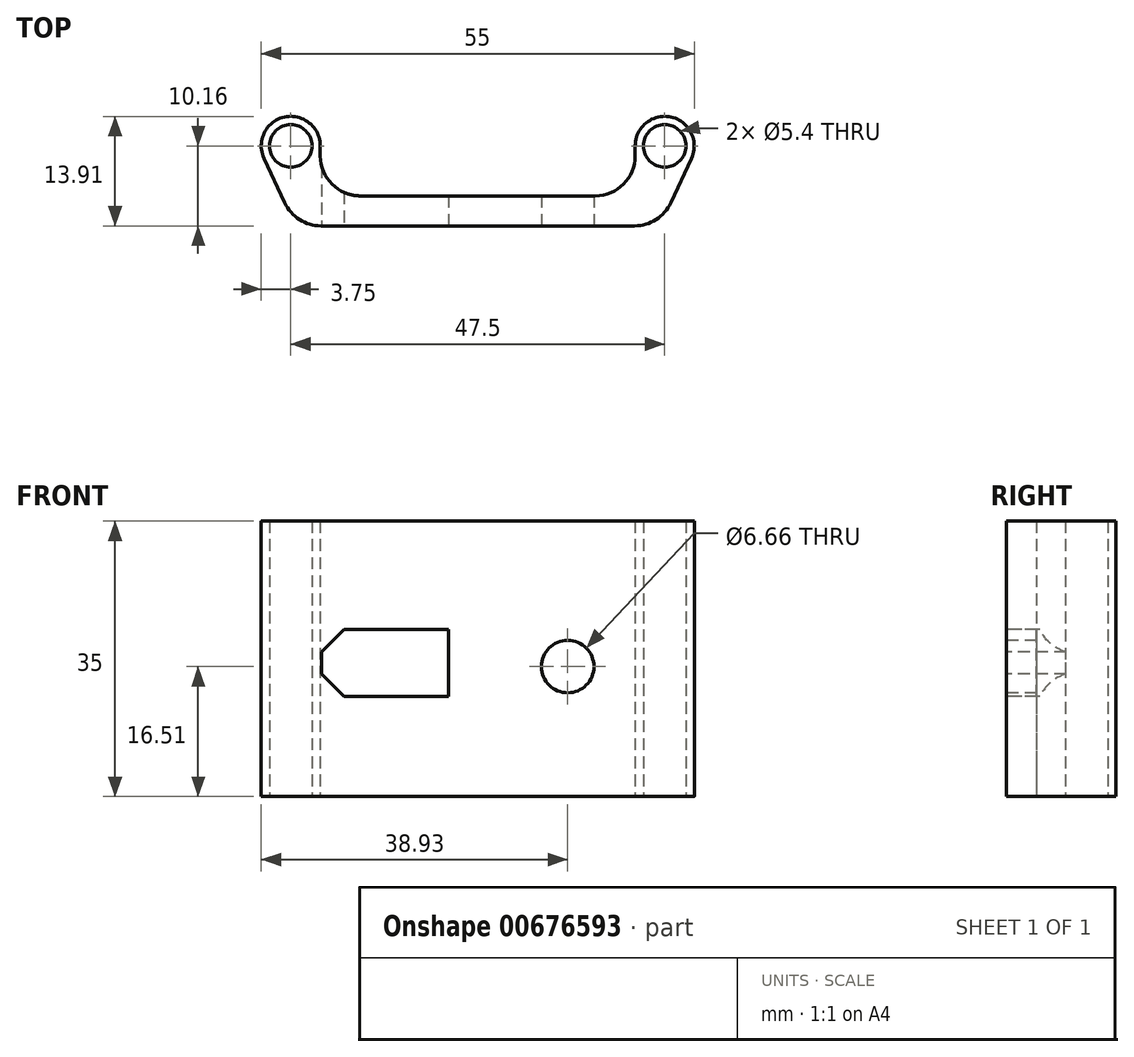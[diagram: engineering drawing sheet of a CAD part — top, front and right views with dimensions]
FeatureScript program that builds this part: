
annotation { "Feature Type Name" : "Feature", "Feature Type Description" : "" }
export const myFeature = defineFeature(function(context is Context, id is Id, definition is map)
    precondition{}
    {
        {
            var Q0;
            Q0=qCreatedBy(makeId("Top.planeOp"),FACE);
            var sketch = newSketch(context, id + "F0", { "sketchPlane" : qUnion([Q0])});
            skCircle(sketch, "E0", {"center": v(-23.75, 0) * mm, "radius": 2.7 * mm});
            skCircle(sketch, "E1", {"center": v(23.75, 0) * mm, "radius": 2.7 * mm});
            skCircle(sketch, "E2", {"center": v(-23.75, 0) * mm, "radius": 3.75 * mm});
            skCircle(sketch, "E3", {"center": v(23.75, 0) * mm, "radius": 3.75 * mm});
            skLineSegment(sketch, "E4", {"start": v(-23.15, -10.16) * mm, "end": v(23.15, -10.16) * mm});
            skLineSegment(sketch, "E5", {"start": v(23.15, -10.16) * mm, "end": v(27.15, -1.58) * mm});
            skLineSegment(sketch, "E6", {"start": v(-23.15, -10.16) * mm, "end": v(-27.15, -1.58) * mm});
            skPoint(sketch, "E7.orphan", {"position": v(27.89, 0) * mm});
            skPoint(sketch, "E8.orphan", {"position": v(-27.89, 0) * mm});
            skLineSegment(sketch, "E9", {"start": v(-20, 0) * mm, "end": v(-20, -6.35) * mm});
            skLineSegment(sketch, "E10", {"start": v(-20, -6.35) * mm, "end": v(20, -6.35) * mm});
            skLineSegment(sketch, "E11", {"start": v(20, -6.35) * mm, "end": v(20, 0) * mm});
            skSolve(sketch);
        }
        {
            var Q0;
            Q0=makeQuery(id+"F0.imprint","IMPRINT",FACE,{"disambiguationData":[TD([[makeQuery(id+"F0.imprint","IMPRINT",EDGE,{"derivedFrom":sQuery(id+"F0.wireOp",EDGE,"E4")}),1.0]])]});
            var Q1;
            Q1=makeQuery(id+"F0.imprint","IMPRINT",FACE,{"disambiguationData":[TD([[makeQuery(id+"F0.imprint","IMPRINT",EDGE,{"derivedFrom":sQuery(id+"F0.wireOp",EDGE,"E0")}),-1.0]])]});
            var Q2;
            Q2=makeQuery(id+"F0.imprint","IMPRINT",FACE,{"disambiguationData":[TD([[makeQuery(id+"F0.imprint","IMPRINT",EDGE,{"derivedFrom":sQuery(id+"F0.wireOp",EDGE,"E1")}),-1.0]])]});
            extrude(context, id + "F1", {"entities" : qUnion([Q0, Q1, Q2]), "depth" : 35 * mm, "offsetDistance" : 25.4 * mm});
        }
        {
            var Q0;
            Q0=makeQuery(id+"F1.opExtrude","SWEPT_FACE",FACE,{"disambiguationData":[OSD([sQuery(id+"F0.wireOp",EDGE,"E4")])]});
            var sketch = newSketch(context, id + "F2", { "sketchPlane" : qUnion([Q0])});
            skCircle(sketch, "E12", {"center": v(11.43, 16.51) * mm, "radius": 3.33 * mm});
            skLineSegment(sketch, "E13.bottom", {"start": v(-3.68, 21.23) * mm, "end": v(-19.82, 21.23) * mm});
            skLineSegment(sketch, "E13.top", {"start": v(-3.68, 12.7) * mm, "end": v(-19.82, 12.7) * mm});
            skLineSegment(sketch, "E13.left", {"start": v(-3.68, 21.23) * mm, "end": v(-3.68, 12.7) * mm});
            skLineSegment(sketch, "E13.right", {"start": v(-19.82, 21.23) * mm, "end": v(-19.82, 12.7) * mm});
            skLineSegment(sketch, "E14", {"start": v(-16.97, 21.23) * mm, "end": v(-19.82, 18.38) * mm});
            skLineSegment(sketch, "E15", {"start": v(-16.97, 12.7) * mm, "end": v(-19.82, 15.55) * mm});
            skSolve(sketch);
        }
        {
            var Q0;
            {var subQ3=sQuery(id+"F2.wireOp",EDGE,"E13.left");Q0=makeQuery(id+"F2.imprint","IMPRINT",FACE,{"disambiguationData":[TD([[makeQuery(id+"F2.imprint","IMPRINT",EDGE,{"derivedFrom":subQ3}),-1.0]])]});}
            var Q1;
            Q1=makeQuery(id+"F2.imprint","IMPRINT",FACE,{"disambiguationData":[TD([[makeQuery(id+"F2.imprint","IMPRINT",EDGE,{"derivedFrom":sQuery(id+"F2.wireOp",EDGE,"E12")}),1.0]])]});
            extrude(context, id + "F3", {"entities" : qUnion([Q0, Q1]), "operationType" : NewBodyOperationType.REMOVE, "endBound" : BoundingType.THROUGH_ALL, "oppositeDirection" : true, "depth" : 25.4 * mm, "offsetDistance" : 25.4 * mm});
        }
        {
            var Q0;
            Q0=makeQuery(id+"F1.opExtrude","SWEPT_EDGE",EDGE,{"disambiguationData":[OSD([sQuery(id+"F0.wireOp",EDGE,"E9"),sQuery(id+"F0.wireOp",EDGE,"E10")])]});
            var Q1;
            Q1=makeQuery(id+"F1.opExtrude","SWEPT_EDGE",EDGE,{"disambiguationData":[OSD([sQuery(id+"F0.wireOp",EDGE,"E10"),sQuery(id+"F0.wireOp",EDGE,"E11")])]});
            fillet(context, id + "F4", {"entities" : qUnion([Q0, Q1]), "radius" : 5.08 * mm, "tangentPropagation" : true, "allowEdgeOverflow" : false});
        }
        {
            var Q0;
            Q0=makeQuery(id+"F1.opExtrude","SWEPT_EDGE",EDGE,{"disambiguationData":[OSD([sQuery(id+"F0.wireOp",EDGE,"E4"),sQuery(id+"F0.wireOp",EDGE,"E6")])]});
            var Q1;
            Q1=makeQuery(id+"F1.opExtrude","SWEPT_EDGE",EDGE,{"disambiguationData":[OSD([sQuery(id+"F0.wireOp",EDGE,"E4"),sQuery(id+"F0.wireOp",EDGE,"E5")])]});
            fillet(context, id + "F5", {"entities" : qUnion([Q0, Q1]), "radius" : 5.08 * mm, "tangentPropagation" : true, "allowEdgeOverflow" : false});
        }
    });
